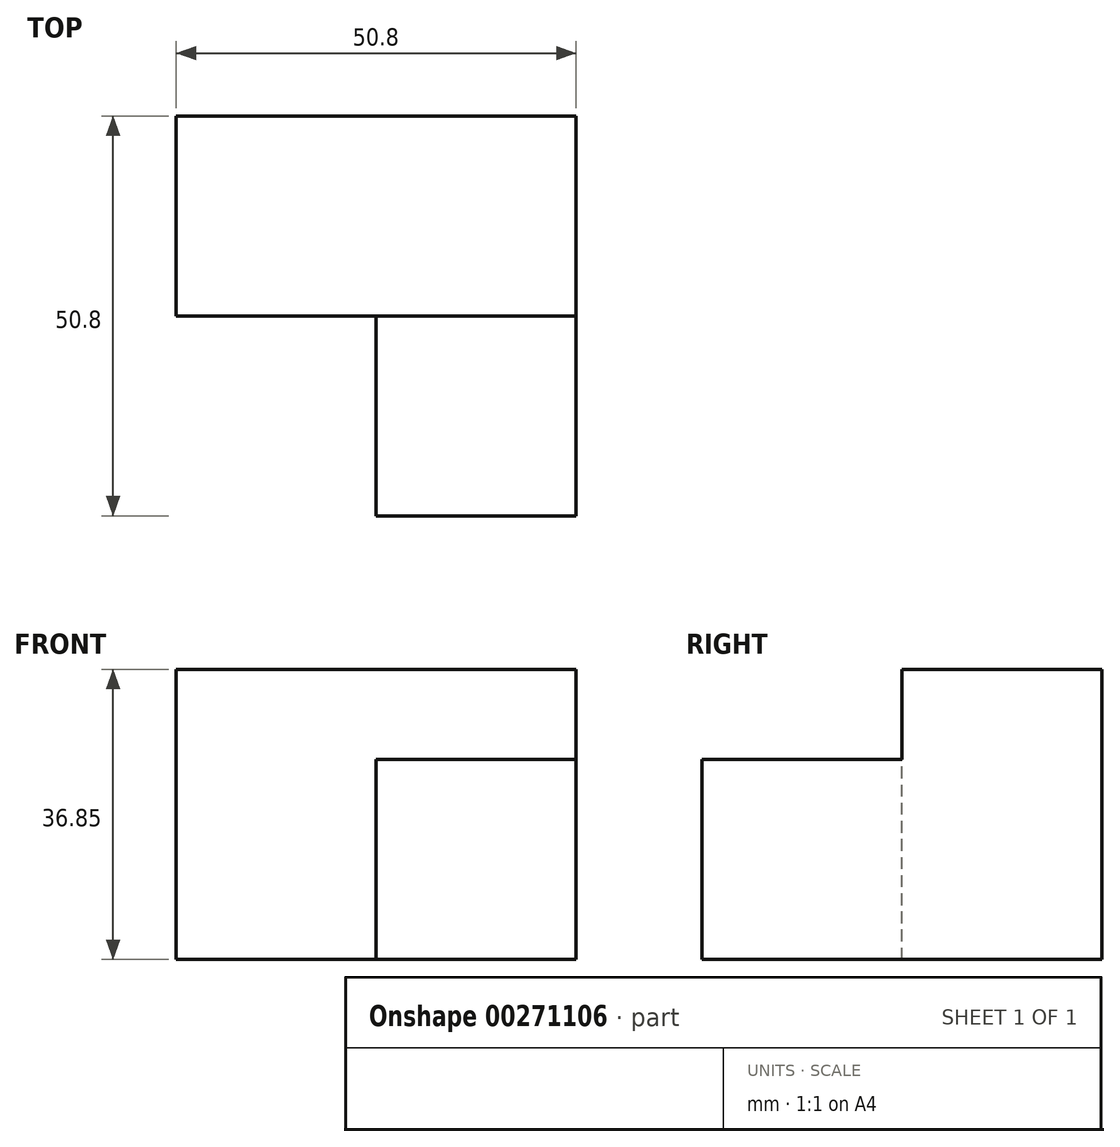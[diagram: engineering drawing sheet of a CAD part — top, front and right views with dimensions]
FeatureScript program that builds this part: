
annotation { "Feature Type Name" : "Feature", "Feature Type Description" : "" }
export const myFeature = defineFeature(function(context is Context, id is Id, definition is map)
    precondition{}
    {
        {
            var Q0;
            Q0=qCreatedBy(makeId("Front.planeOp"),FACE);
            var sketch = newSketch(context, id + "F0", { "sketchPlane" : qUnion([Q0])});
            skLineSegment(sketch, "E0.bottom", {"start": v(0, 0) * mm, "end": v(-50.8, 0) * mm});
            skLineSegment(sketch, "E0.top", {"start": v(0, 36.85) * mm, "end": v(-50.8, 36.85) * mm});
            skLineSegment(sketch, "E0.left", {"start": v(0, 0) * mm, "end": v(0, 36.85) * mm});
            skLineSegment(sketch, "E0.right", {"start": v(-50.8, 0) * mm, "end": v(-50.8, 36.85) * mm});
            skSolve(sketch);
        }
        {
            var Q0;
            Q0 = qSketchRegion(id + "F0", true);
            extrude(context, id + "F1", {"entities" : qUnion([Q0]), "depth" : 25.4 * mm});
        }
        {
            var Q0;
            Q0=makeQuery(id+"F1.opExtrude","CAP_FACE",FACE,{"disambiguationData":[OSD([sQuery(id+"F0.wireOp",EDGE,"E0.bottom"),sQuery(id+"F0.wireOp",EDGE,"E0.top"),sQuery(id+"F0.wireOp",EDGE,"E0.left"),sQuery(id+"F0.wireOp",EDGE,"E0.right")])],"isStart":false});
            var sketch = newSketch(context, id + "F2", { "sketchPlane" : qUnion([Q0])});
            skLineSegment(sketch, "E1", {"start": v(0, 0) * mm, "end": v(-25.4, 0) * mm});
            skLineSegment(sketch, "E2", {"start": v(-25.4, 0) * mm, "end": v(-25.4, 25.4) * mm});
            skLineSegment(sketch, "E3", {"start": v(-25.4, 25.4) * mm, "end": v(0, 25.4) * mm});
            skLineSegment(sketch, "E4", {"start": v(0, 25.4) * mm, "end": v(0, 0) * mm});
            skSolve(sketch);
        }
        {
            var Q0;
            Q0 = qSketchRegion(id + "F2", true);
            extrude(context, id + "F3", {"entities" : qUnion([Q0]), "operationType" : NewBodyOperationType.ADD, "depth" : 25.4 * mm});
        }
    });
